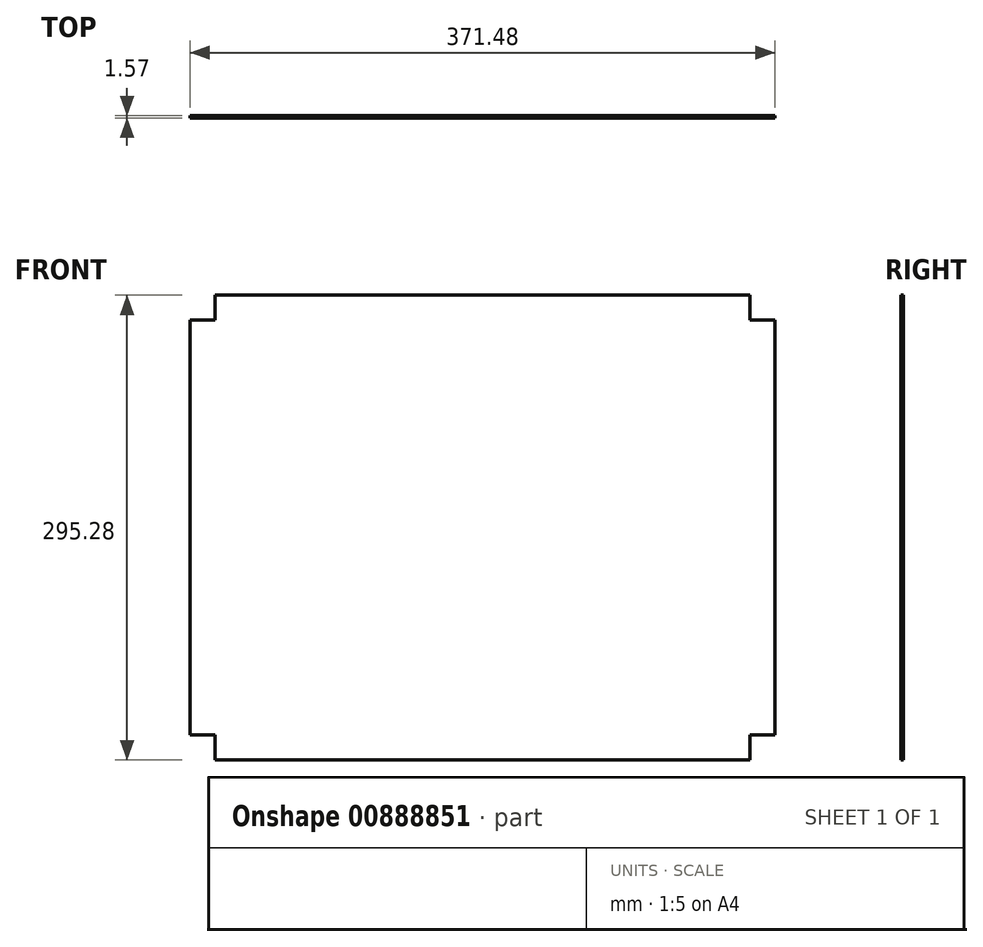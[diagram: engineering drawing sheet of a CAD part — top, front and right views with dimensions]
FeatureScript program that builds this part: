
annotation { "Feature Type Name" : "Feature", "Feature Type Description" : "" }
export const myFeature = defineFeature(function(context is Context, id is Id, definition is map)
    precondition{}
    {
        {
            var Q0;
            Q0=qCreatedBy(makeId("Front.planeOp"),FACE);
            var sketch = newSketch(context, id + "F0", { "sketchPlane" : qUnion([Q0])});
            skLineSegment(sketch, "E0.bottom", {"start": v(169.86, -147.64) * mm, "end": v(-169.86, -147.64) * mm});
            skLineSegment(sketch, "E0.top", {"start": v(169.86, 147.64) * mm, "end": v(-169.86, 147.64) * mm});
            skLineSegment(sketch, "E0.left", {"start": v(185.74, -131.76) * mm, "end": v(185.74, 131.76) * mm});
            skLineSegment(sketch, "E0.right", {"start": v(-185.74, -131.76) * mm, "end": v(-185.74, 131.76) * mm});
            skPoint(sketch, "E0.middle", {"position": v(0, 0) * mm});
            skLineSegment(sketch, "E1", {"start": v(-169.86, -147.64) * mm, "end": v(-169.86, -131.76) * mm});
            skLineSegment(sketch, "E2", {"start": v(-169.86, -131.76) * mm, "end": v(-185.74, -131.76) * mm});
            skLineSegment(sketch, "E3", {"start": v(169.86, -131.76) * mm, "end": v(169.86, -147.64) * mm});
            skLineSegment(sketch, "E4", {"start": v(169.86, -131.76) * mm, "end": v(185.74, -131.76) * mm});
            skLineSegment(sketch, "E5", {"start": v(185.74, -131.76) * mm, "end": v(185.74, -131.76) * mm});
            skLineSegment(sketch, "E6", {"start": v(169.86, 131.76) * mm, "end": v(185.74, 131.76) * mm});
            skLineSegment(sketch, "E7", {"start": v(169.86, 131.76) * mm, "end": v(169.86, 147.64) * mm});
            skLineSegment(sketch, "E8", {"start": v(-169.86, 131.76) * mm, "end": v(-169.86, 147.64) * mm});
            skLineSegment(sketch, "E9", {"start": v(-169.86, 147.64) * mm, "end": v(-169.86, 147.64) * mm});
            skLineSegment(sketch, "E10", {"start": v(-169.86, 131.76) * mm, "end": v(-185.74, 131.76) * mm});
            skPoint(sketch, "E11.orphan", {"position": v(185.74, -147.64) * mm});
            skPoint(sketch, "E12.orphan", {"position": v(185.74, 147.64) * mm});
            skPoint(sketch, "E13.orphan", {"position": v(-185.74, 147.64) * mm});
            skPoint(sketch, "E14.orphan", {"position": v(-185.74, -147.64) * mm});
            skSolve(sketch);
        }
        {
            var Q0;
            Q0=makeQuery(id+"F0.imprint","IMPRINT",FACE,{"disambiguationData":[TD([[makeQuery(id+"F0.imprint","IMPRINT",EDGE,{"derivedFrom":sQuery(id+"F0.wireOp",EDGE,"E0.bottom")}),-1.0]])]});
            extrude(context, id + "F1", {"entities" : qUnion([Q0]), "depth" : 1.57 * mm, "offsetDistance" : 25.4 * mm});
        }
    });
